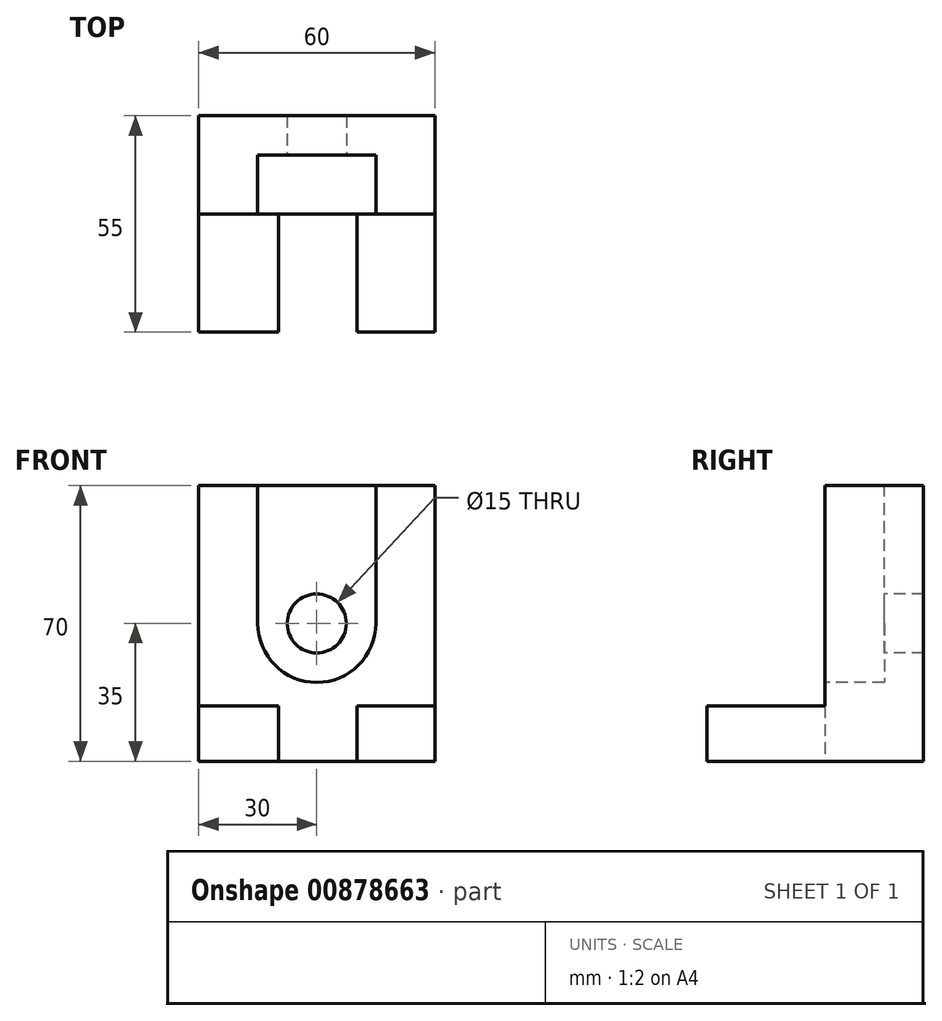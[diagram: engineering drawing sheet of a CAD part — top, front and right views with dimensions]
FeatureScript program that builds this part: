
annotation { "Feature Type Name" : "Feature", "Feature Type Description" : "" }
export const myFeature = defineFeature(function(context is Context, id is Id, definition is map)
    precondition{}
    {
        {
            var Q0;
            Q0=qCreatedBy(makeId("Front.planeOp"),FACE);
            var sketch = newSketch(context, id + "F0", { "sketchPlane" : qUnion([Q0])});
            skLineSegment(sketch, "E0.bottom", {"start": v(-30, 35) * mm, "end": v(30, 35) * mm});
            skLineSegment(sketch, "E0.top", {"start": v(-30, -35) * mm, "end": v(30, -35) * mm});
            skLineSegment(sketch, "E0.left", {"start": v(-30, 35) * mm, "end": v(-30, -35) * mm});
            skLineSegment(sketch, "E0.right", {"start": v(30, 35) * mm, "end": v(30, -35) * mm});
            skPoint(sketch, "E0.middle", {"position": v(0, 0) * mm});
            skPoint(sketch, "E1.middle", {"position": v(0, -35) * mm});
            skPoint(sketch, "E2.orphan", {"position": v(10, -45) * mm});
            skPoint(sketch, "E3.orphan", {"position": v(-10, -45) * mm});
            skPoint(sketch, "E1.top.end.orphan", {"position": v(10, -25) * mm});
            skPoint(sketch, "E1.left.end.orphan", {"position": v(-10, -25) * mm});
            skSolve(sketch);
        }
        {
            var Q0;
            Q0 = qSketchRegion(id + "F0", true);
            extrude(context, id + "F1", {"entities" : qUnion([Q0]), "depth" : 25 * mm, "offsetDistance" : 25 * mm});
        }
        {
            var Q0;
            Q0=makeQuery(id+"F1.opExtrude","CAP_FACE",FACE,{"disambiguationData":[OSD([sQuery(id+"F0.wireOp",EDGE,"E0.bottom"),sQuery(id+"F0.wireOp",EDGE,"E0.top"),sQuery(id+"F0.wireOp",EDGE,"E0.left"),sQuery(id+"F0.wireOp",EDGE,"E0.right")])],"isStart":false});
            var sketch = newSketch(context, id + "F2", { "sketchPlane" : qUnion([Q0])});
            skArc(sketch, "E4", {"start": v(-15, 0) * mm, "mid": v(0, -15) * mm, "end": v(15, 0) * mm});
            skLineSegment(sketch, "E5", {"start": v(-15, 0) * mm, "end": v(-15, 35) * mm});
            skLineSegment(sketch, "E6", {"start": v(15, 0) * mm, "end": v(15, 35) * mm});
            skSolve(sketch);
        }
        {
            var Q0;
            Q0 = qSketchRegion(id + "F2", true);
            var Q1;
            Q1=makeQuery(id+"F2.imprint","IMPRINT",FACE,{"disambiguationData":[TD([[makeQuery(id+"F2.imprint","IMPRINT",EDGE,{"derivedFrom":sQuery(id+"F2.wireOp",EDGE,"E4")}),1.0]])]});
            extrude(context, id + "F3", {"entities" : qUnion([Q0, Q1]), "operationType" : NewBodyOperationType.REMOVE, "oppositeDirection" : true, "depth" : 15 * mm, "offsetDistance" : 25 * mm});
        }
        {
            var Q0;
            Q0=qCreatedBy(makeId("Front.planeOp"),FACE);
            var sketch = newSketch(context, id + "F4", { "sketchPlane" : qUnion([Q0])});
            skCircle(sketch, "E7", {"center": v(0, 0) * mm, "radius": 7.5 * mm});
            skSolve(sketch);
        }
        {
            var Q0;
            Q0 = qSketchRegion(id + "F4", true);
            extrude(context, id + "F5", {"entities" : qUnion([Q0]), "operationType" : NewBodyOperationType.ADD, "depth" : 25 * mm, "offsetDistance" : 25 * mm});
        }
        {
            var Q0;
            Q0=makeQuery(id+"F5.opExtrude","CAP_FACE",FACE,{"disambiguationData":[OSD([sQuery(id+"F4.wireOp",EDGE,"E7")])],"isStart":false});
            extrude(context, id + "F6", {"entities" : qUnion([Q0]), "operationType" : NewBodyOperationType.REMOVE, "endBound" : BoundingType.THROUGH_ALL, "oppositeDirection" : true, "depth" : 25 * mm, "offsetDistance" : 25 * mm});
        }
        {
            var Q0;
            Q0=makeQuery(id+"F1.opExtrude","CAP_FACE",FACE,{"disambiguationData":[OSD([sQuery(id+"F0.wireOp",EDGE,"E0.bottom"),sQuery(id+"F0.wireOp",EDGE,"E0.top"),sQuery(id+"F0.wireOp",EDGE,"E0.left"),sQuery(id+"F0.wireOp",EDGE,"E0.right")])],"isStart":false});
            var sketch = newSketch(context, id + "F7", { "sketchPlane" : qUnion([Q0])});
            skLineSegment(sketch, "E8", {"start": v(-30, -21) * mm, "end": v(30, -21) * mm});
            skLineSegment(sketch, "E9", {"start": v(10.27, -21) * mm, "end": v(10.27, -35) * mm});
            skLineSegment(sketch, "E10", {"start": v(10.27, -35) * mm, "end": v(30, -35) * mm});
            skLineSegment(sketch, "E11", {"start": v(30, -35) * mm, "end": v(30, -21) * mm});
            skLineSegment(sketch, "E12", {"start": v(-9.73, -21) * mm, "end": v(-9.73, -35) * mm});
            skLineSegment(sketch, "E13", {"start": v(-9.73, -35) * mm, "end": v(-30, -35) * mm});
            skLineSegment(sketch, "E14", {"start": v(-30, -35) * mm, "end": v(-30, -21) * mm});
            skSolve(sketch);
        }
        {
            var Q0;
            Q0 = qSketchRegion(id + "F7", true);
            extrude(context, id + "F8", {"entities" : qUnion([Q0]), "operationType" : NewBodyOperationType.ADD, "depth" : 30 * mm, "offsetDistance" : 25 * mm});
        }
    });
